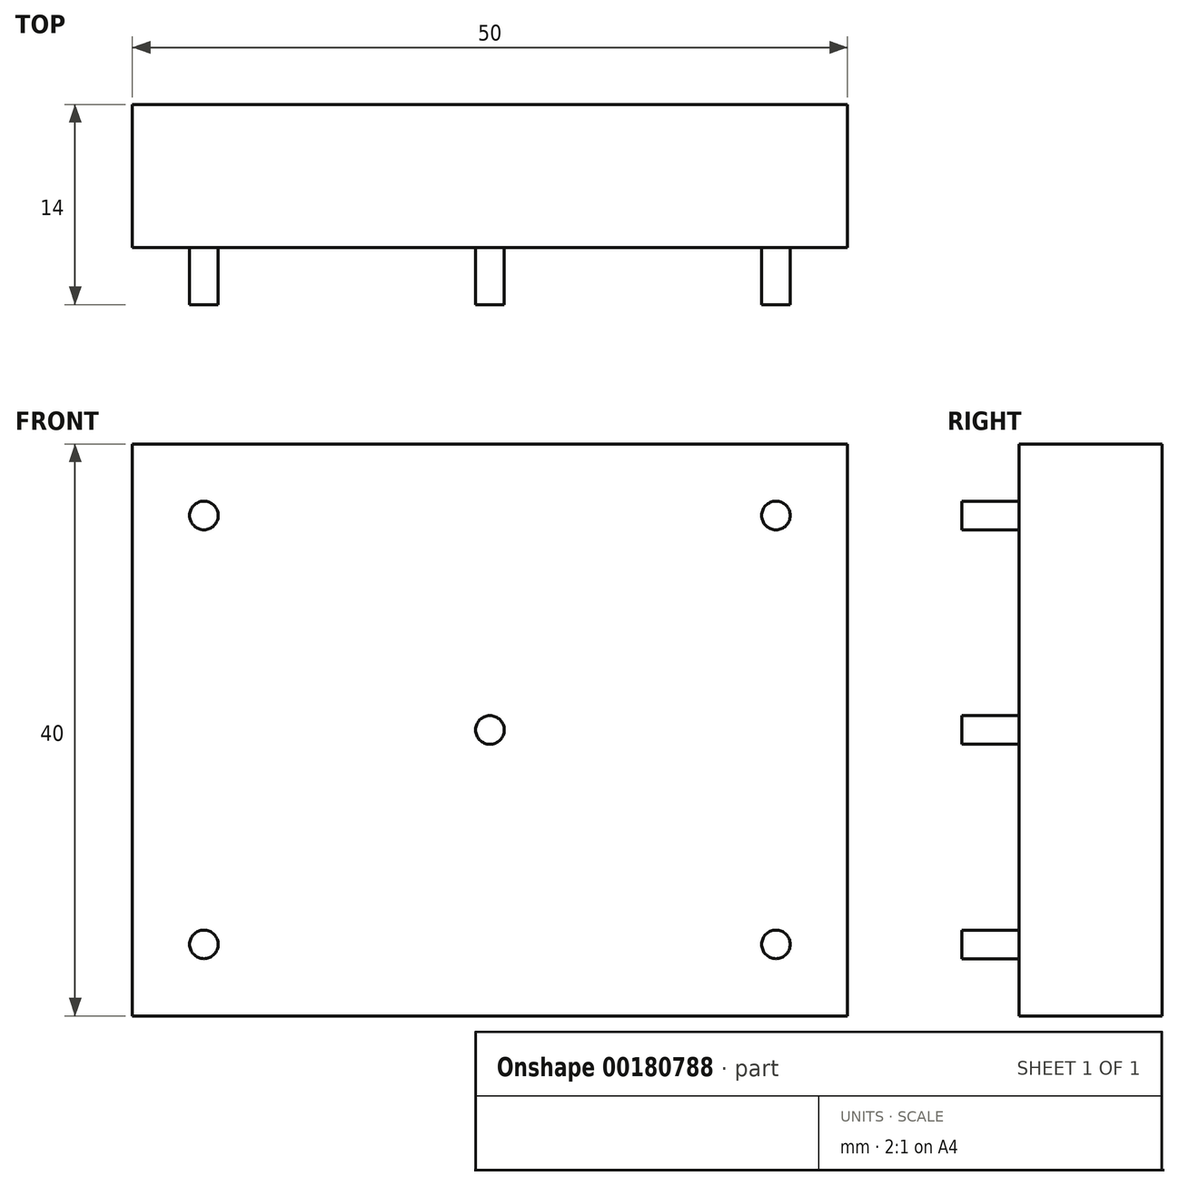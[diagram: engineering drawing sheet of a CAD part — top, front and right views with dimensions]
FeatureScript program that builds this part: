
annotation { "Feature Type Name" : "Feature", "Feature Type Description" : "" }
export const myFeature = defineFeature(function(context is Context, id is Id, definition is map)
    precondition{}
    {
        {
            var Q0;
            Q0=qCreatedBy(makeId("Right.planeOp"),FACE);
            var sketch = newSketch(context, id + "F0", { "sketchPlane" : qUnion([Q0])});
            skLineSegment(sketch, "E0.bottom", {"start": v(5, -20) * mm, "end": v(-5, -20) * mm});
            skLineSegment(sketch, "E0.top", {"start": v(5, 20) * mm, "end": v(-5, 20) * mm});
            skLineSegment(sketch, "E0.left", {"start": v(5, -20) * mm, "end": v(5, 20) * mm});
            skLineSegment(sketch, "E0.right", {"start": v(-5, -20) * mm, "end": v(-5, 20) * mm});
            skPoint(sketch, "E0.middle", {"position": v(0, 0) * mm});
            skSolve(sketch);
        }
        {
            var Q0;
            Q0=makeQuery(id+"F0.imprint","IMPRINT",FACE,{"disambiguationData":[TD([[makeQuery(id+"F0.imprint","IMPRINT",EDGE,{"derivedFrom":sQuery(id+"F0.wireOp",EDGE,"E0.bottom")}),-1.0]])]});
            extrude(context, id + "F1", {"entities" : qUnion([Q0]), "depth" : 25 * mm, "hasSecondDirection" : true, "secondDirectionOppositeDirection" : true, "secondDirectionDepth" : 25 * mm});
        }
        {
            var Q0;
            Q0=makeQuery(id+"F1.opExtrude","SWEPT_FACE",FACE,{"disambiguationData":[OSD([sQuery(id+"F0.wireOp",EDGE,"E0.right")])]});
            var sketch = newSketch(context, id + "F2", { "sketchPlane" : qUnion([Q0])});
            skCircle(sketch, "E1", {"center": v(0, 0) * mm, "radius": 1 * mm});
            skCircle(sketch, "E2", {"center": v(-20, 15) * mm, "radius": 1 * mm});
            skCircle(sketch, "E3", {"center": v(-20, -15) * mm, "radius": 1 * mm});
            skCircle(sketch, "E4", {"center": v(20, -15) * mm, "radius": 1 * mm});
            skCircle(sketch, "E5", {"center": v(20, 15) * mm, "radius": 1 * mm});
            skSolve(sketch);
        }
        {
            var Q0;
            Q0 = qSketchRegion(id + "F2", true);
            extrude(context, id + "F3", {"entities" : qUnion([Q0]), "operationType" : NewBodyOperationType.ADD, "depth" : 4 * mm});
        }
    });
